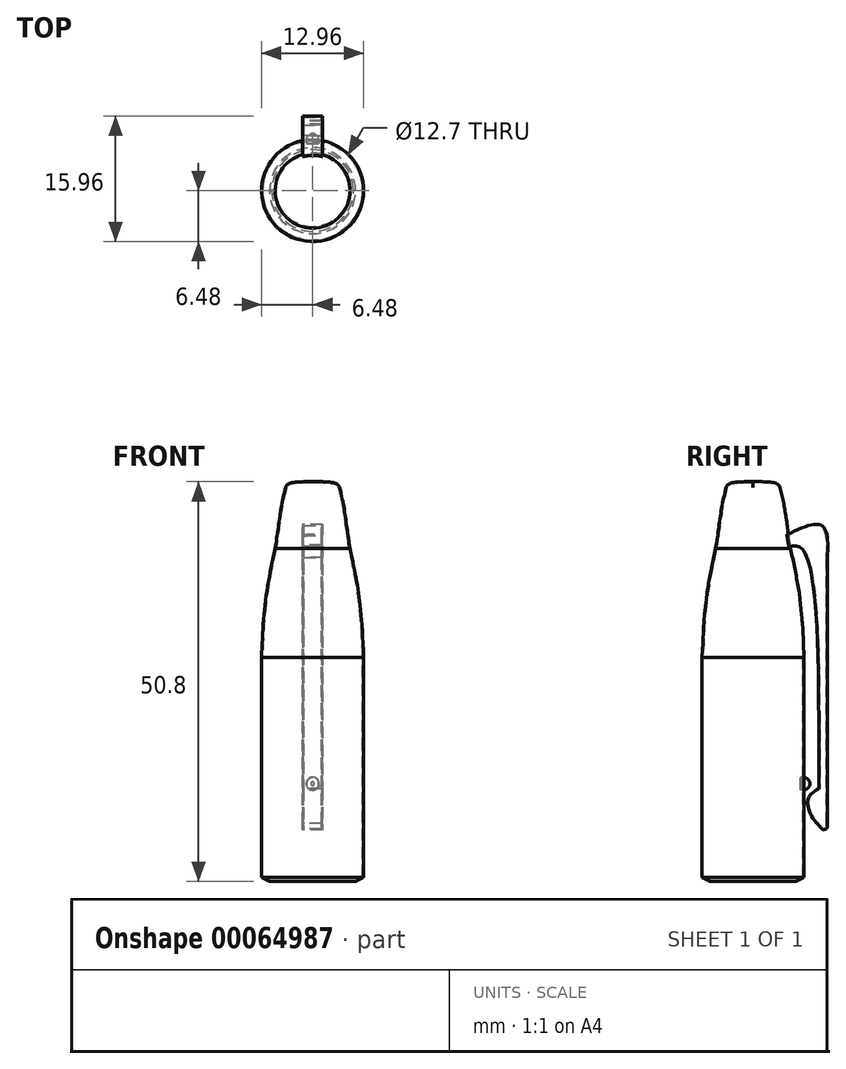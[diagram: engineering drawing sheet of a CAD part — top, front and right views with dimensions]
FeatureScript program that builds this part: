
annotation { "Feature Type Name" : "Feature", "Feature Type Description" : "" }
export const myFeature = defineFeature(function(context is Context, id is Id, definition is map)
    precondition{}
    {
        {
            var Q0;
            Q0=qCreatedBy(makeId("Front.planeOp"),FACE);
            var sketch = newSketch(context, id + "F0", { "sketchPlane" : qUnion([Q0])});
            skLineSegment(sketch, "E0", {"start": v(-22.13, 50.8) * mm, "end": v(38.53, 50.8) * mm, "construction": true});
            skLineSegment(sketch, "E1", {"start": v(6.48, 57.61) * mm, "end": v(6.48, -6.81) * mm, "construction": true});
            skLineSegment(sketch, "E2", {"start": v(-7.17, 28.45) * mm, "end": v(21.94, 28.45) * mm, "construction": true});
            skLineSegment(sketch, "E3", {"start": v(-7.06, 42.3) * mm, "end": v(23.04, 42.3) * mm, "construction": true});
            skLineSegment(sketch, "E4", {"start": v(4.76, 58.76) * mm, "end": v(4.76, -11.65) * mm, "construction": true});
            skLineSegment(sketch, "E5", {"start": v(0, 0) * mm, "end": v(5.46, 0) * mm});
            skFitSpline(sketch, "E6", {"points": [v(5.46, 0) * mm, v(6.48, 0.55) * mm], "startDerivative": vector(1.02, 0.55) * mm, "endDerivative": vector(1.02, 0.55) * mm});
            skLineSegment(sketch, "E7", {"start": v(6.48, 0.55) * mm, "end": v(6.48, 28.45) * mm});
            skFitSpline(sketch, "E8", {"points": [v(6.48, 28.45) * mm, v(4.76, 42.3) * mm], "startDerivative": vector(-0.76, 22.2) * mm, "endDerivative": vector(-2.83, 13.7) * mm});
            skLineSegment(sketch, "E9", {"start": v(3.43, 61.41) * mm, "end": v(3.43, -2.08) * mm, "construction": true});
            skFitSpline(sketch, "E10", {"points": [v(0, 50.8) * mm, v(3.43, 50.08) * mm], "startDerivative": vector(6.34, 0) * mm, "endDerivative": vector(0.53, -2.16) * mm});
            skFitSpline(sketch, "E11", {"points": [v(4.76, 42.3) * mm, v(3.43, 50.08) * mm], "startDerivative": vector(-1.33, 7.8) * mm, "endDerivative": vector(-2.23, 8.7) * mm});
            skLineSegment(sketch, "E12", {"start": v(0, 50.8) * mm, "end": v(0, 0) * mm});
            skSolve(sketch);
        }
        {
            var Q0;
            Q0 = qSketchRegion(id + "F0", true);
            var Q1;
            Q1=sQuery(id+"F0.wireOp",EDGE,"E12");
            revolve(context, id + "F1", {"entities" : qUnion([Q0]), "axis" : qUnion([Q1]), "revolveType" : RevolveType.FULL});
        }
        {
            var Q0;
            Q0=qCreatedBy(makeId("Right.planeOp"),FACE);
            var sketch = newSketch(context, id + "F2", { "sketchPlane" : qUnion([Q0])});
            skFitSpline(sketch, "E13", {"points": [v(3.81, 42.3) * mm, v(6.22, 42.27) * mm, v(8.35, 11.81) * mm], "startDerivative": vector(10.38, 3.24) * mm, "endDerivative": vector(0.34, -38.61) * mm});
            skFitSpline(sketch, "E14", {"points": [v(8.35, 11.81) * mm, v(7.12, 10.83) * mm, v(7.02, 9.28) * mm, v(8.83, 6.59) * mm], "startDerivative": vector(-5.12, -3.04) * mm, "endDerivative": vector(7.2, -7) * mm});
            skFitSpline(sketch, "E15", {"points": [v(8.83, 6.59) * mm, v(9.45, 7.37) * mm], "startDerivative": vector(1.78, 0.13) * mm, "endDerivative": vector(-0.04, 1.66) * mm});
            skFitSpline(sketch, "E16", {"points": [v(9.45, 7.37) * mm, v(9.45, 41.15) * mm], "startDerivative": vector(0, 33.78) * mm, "endDerivative": vector(0, 33.78) * mm});
            skPoint(sketch, "E17.end.orphan", {"position": v(9.45, 44.96) * mm});
            skFitSpline(sketch, "E18", {"points": [v(9.45, 41.15) * mm, v(8.73, 45.22) * mm, v(3.67, 43.75) * mm], "startDerivative": vector(0.36, 11.35) * mm, "endDerivative": vector(-11.67, -5.8) * mm});
            skLineSegment(sketch, "E19", {"start": v(3.81, 42.3) * mm, "end": v(3.67, 43.75) * mm});
            skSolve(sketch);
        }
        {
            var Q0;
            Q0 = qSketchRegion(id + "F2", true);
            extrude(context, id + "F3", {"entities" : qUnion([Q0]), "operationType" : NewBodyOperationType.ADD, "depth" : 1.27 * mm, "hasSecondDirection" : true, "secondDirectionOppositeDirection" : true, "secondDirectionDepth" : 1.27 * mm});
        }
        {
            var Q0;
            Q0=makeQuery(id+"F1.opRevolve","SWEPT_FACE",FACE,{"disambiguationData":[OSD([sQuery(id+"F0.wireOp",EDGE,"E5")])]});
            shell(context, id + "F4", {"entities" : qUnion([Q0]), "thickness" : 0.13 * mm});
        }
        {
            var Q0;
            Q0=qCreatedBy(makeId("Right.planeOp"),FACE);
            var sketch = newSketch(context, id + "F5", { "sketchPlane" : qUnion([Q0])});
            skLineSegment(sketch, "E20", {"start": v(6, 12.43) * mm, "end": v(7.23, 12.43) * mm});
            skLineSegment(sketch, "E21", {"start": v(6, 12.43) * mm, "end": v(6, 11.66) * mm});
            skArc(sketch, "E22", {"start": v(6, 11.66) * mm, "mid": v(6.8, 11.75) * mm, "end": v(7.23, 12.43) * mm});
            skSolve(sketch);
        }
        {
            var Q0;
            Q0 = qSketchRegion(id + "F5", true);
            var Q1;
            Q1=sQuery(id+"F5.wireOp",EDGE,"E20");
            revolve(context, id + "F6", {"operationType" : NewBodyOperationType.ADD, "entities" : qUnion([Q0]), "axis" : qUnion([Q1]), "revolveType" : RevolveType.FULL});
        }
    });
